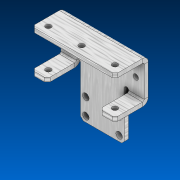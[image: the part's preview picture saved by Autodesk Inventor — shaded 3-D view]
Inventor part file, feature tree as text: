
AUTODESK INVENTOR PART (.ipt)
format: ipt  version: 2022.2 (Build 262287000, 287)  size: 154,112 bytes
history: native  units: in
note: dims shown in document units (in); Inventor stores cm internally (conversion verified against a paired STEP export)
features: chamfer x1
ambient origin geometry x8: Origin, YZ Plane, XZ Plane, XY Plane, X Axis, Y Axis, Z Axis, Center Point
bodies: Solid1 (feature_tree)
feature tree (1):
  chamfer  "Chamfer1"  [1 undecoded]
note: 1 required parameter value undecoded (feature->parameter linkage not recoverable at this tier; creation-order binding heuristic only, values carry confidence <= 0.55)
